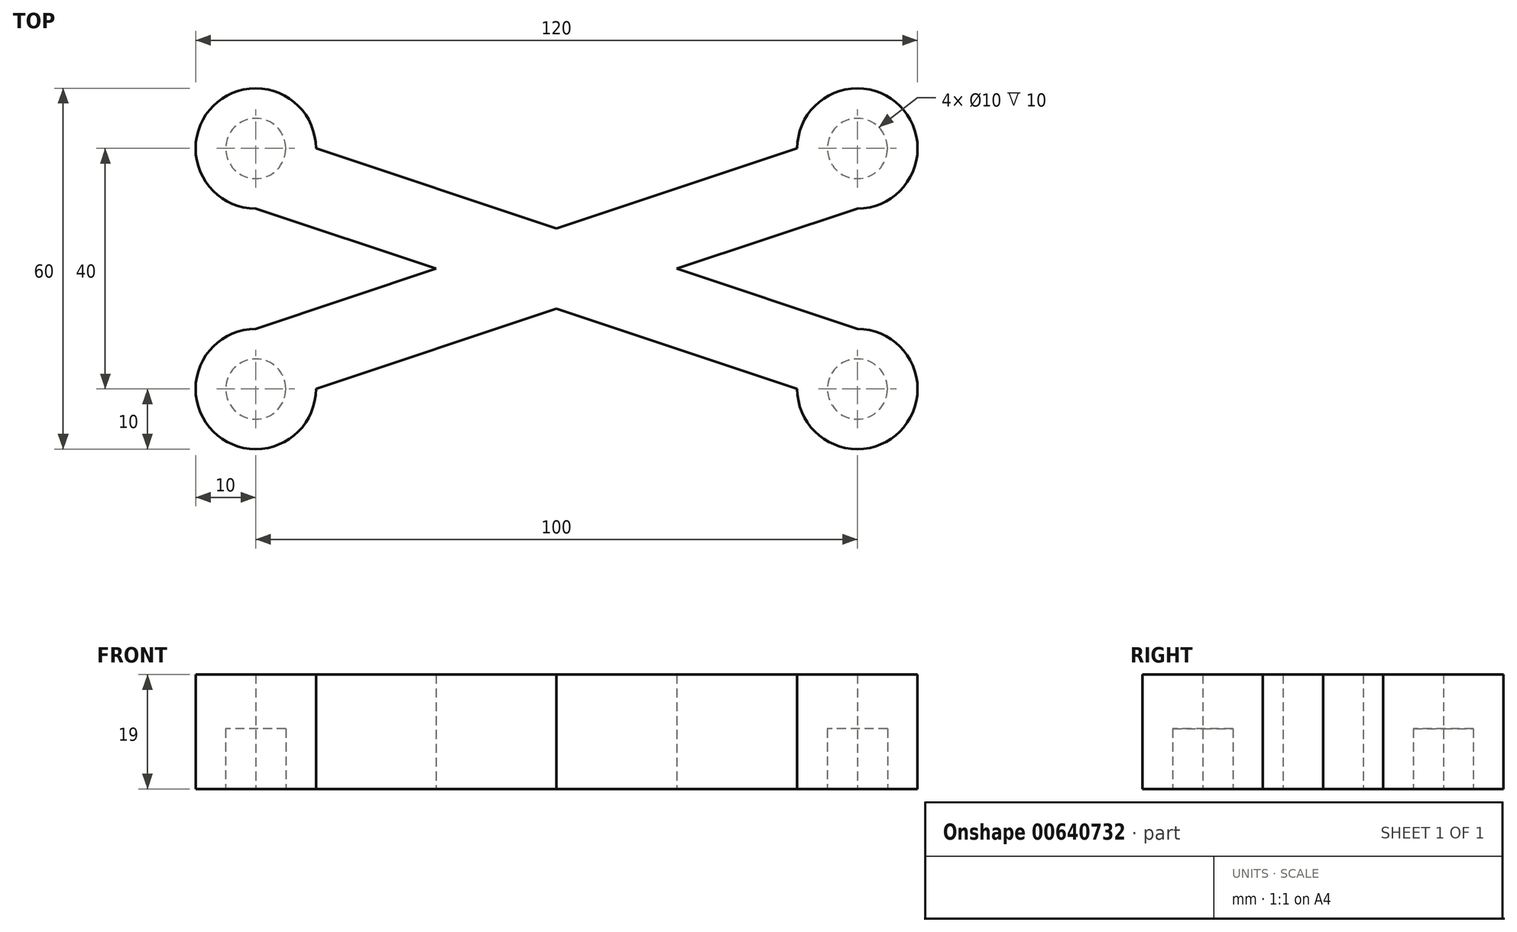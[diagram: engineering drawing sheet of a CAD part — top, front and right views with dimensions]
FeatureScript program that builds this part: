
annotation { "Feature Type Name" : "Feature", "Feature Type Description" : "" }
export const myFeature = defineFeature(function(context is Context, id is Id, definition is map)
    precondition{}
    {
        {
            var Q0;
            Q0=qCreatedBy(makeId("Top.planeOp"),FACE);
            var sketch = newSketch(context, id + "F0", { "sketchPlane" : qUnion([Q0])});
            skLineSegment(sketch, "E0.bottom", {"start": v(-25, 10) * mm, "end": v(25, 10) * mm});
            skLineSegment(sketch, "E0.top", {"start": v(-25, -10) * mm, "end": v(25, -10) * mm});
            skLineSegment(sketch, "E0.left", {"start": v(-25, 10) * mm, "end": v(-25, -10) * mm});
            skLineSegment(sketch, "E0.right", {"start": v(25, 10) * mm, "end": v(25, -10) * mm});
            skPoint(sketch, "E0.middle", {"position": v(0, 0) * mm});
            skLineSegment(sketch, "E1.bottom", {"start": v(0, 0) * mm, "end": v(-50, 0) * mm});
            skLineSegment(sketch, "E1.top", {"start": v(0, 20) * mm, "end": v(-50, 20) * mm});
            skLineSegment(sketch, "E1.left", {"start": v(0, 0) * mm, "end": v(0, 20) * mm});
            skLineSegment(sketch, "E1.right", {"start": v(-50, 0) * mm, "end": v(-50, 20) * mm});
            skPoint(sketch, "E1.middle", {"position": v(-25, 10) * mm});
            skLineSegment(sketch, "E2.bottom", {"start": v(0, 0) * mm, "end": v(50, 0) * mm});
            skLineSegment(sketch, "E2.top", {"start": v(0, 20) * mm, "end": v(50, 20) * mm});
            skLineSegment(sketch, "E2.right", {"start": v(50, 0) * mm, "end": v(50, 20) * mm});
            skPoint(sketch, "E2.middle", {"position": v(25, 10) * mm});
            skLineSegment(sketch, "E3.bottom", {"start": v(-50, 0) * mm, "end": v(0, 0) * mm});
            skLineSegment(sketch, "E3.top", {"start": v(-50, -20) * mm, "end": v(0, -20) * mm});
            skLineSegment(sketch, "E3.left", {"start": v(-50, 0) * mm, "end": v(-50, -20) * mm});
            skLineSegment(sketch, "E3.right", {"start": v(0, 0) * mm, "end": v(0, -20) * mm});
            skPoint(sketch, "E3.middle", {"position": v(-25, -10) * mm});
            skLineSegment(sketch, "E4.bottom", {"start": v(50, 0) * mm, "end": v(0, 0) * mm});
            skLineSegment(sketch, "E4.top", {"start": v(50, -20) * mm, "end": v(0, -20) * mm});
            skLineSegment(sketch, "E4.left", {"start": v(50, 0) * mm, "end": v(50, -20) * mm});
            skPoint(sketch, "E4.middle", {"position": v(25, -10) * mm});
            skCircle(sketch, "E5", {"center": v(-50, 20) * mm, "radius": 10 * mm});
            skCircle(sketch, "E6", {"center": v(-50, -20) * mm, "radius": 10 * mm});
            skCircle(sketch, "E7", {"center": v(50, -20) * mm, "radius": 10 * mm});
            skCircle(sketch, "E8", {"center": v(50, 20) * mm, "radius": 10 * mm});
            skLineSegment(sketch, "E9", {"start": v(-40, 20) * mm, "end": v(50, -10) * mm});
            skLineSegment(sketch, "E10", {"start": v(50, -10) * mm, "end": v(40, -20) * mm});
            skLineSegment(sketch, "E11", {"start": v(-50, 10) * mm, "end": v(40, -20) * mm});
            skLineSegment(sketch, "E12", {"start": v(-50, -10) * mm, "end": v(40, 20) * mm});
            skLineSegment(sketch, "E13", {"start": v(40, 20) * mm, "end": v(50, 10) * mm});
            skLineSegment(sketch, "E14", {"start": v(50, 10) * mm, "end": v(-40, -20) * mm});
            skLineSegment(sketch, "E15", {"start": v(-50, -10) * mm, "end": v(-50, 10) * mm});
            skLineSegment(sketch, "E16", {"start": v(-40, -20) * mm, "end": v(-40, 20) * mm});
            skLineSegment(sketch, "E17", {"start": v(40, -20) * mm, "end": v(40, 20) * mm});
            skSolve(sketch);
        }
        {
            var Q0;
            {var subQ0=sQuery(id+"F0.wireOp",EDGE,"E1.right");Q0=makeQuery(id+"F0.imprint","IMPRINT",FACE,{"disambiguationData":[TD([[makeQuery(id+"F0.imprint","IMPRINT",EDGE,{"derivedFrom":subQ0}),1.0]])]});}
            var Q1;
            {var subQ0=sQuery(id+"F0.wireOp",EDGE,"E2.right");var subQ1=sQuery(id+"F0.wireOp",EDGE,"E2.top");var subQ2=makeQuery(id+"F0.imprint","INTERSECT",VERTEX,{"derivedFrom":[subQ1,subQ0]});Q1=makeQuery(id+"F0.imprint","IMPRINT",FACE,{"disambiguationData":[TD([[makeQuery(id+"F0.imprint","IMPRINT",EDGE,{"disambiguationData":[TD([[subQ2,1.0]])],"derivedFrom":subQ0}),-1.0]])]});}
            var Q2;
            {var subQ0=sQuery(id+"F0.wireOp",EDGE,"E3.left");Q2=makeQuery(id+"F0.imprint","IMPRINT",FACE,{"disambiguationData":[TD([[makeQuery(id+"F0.imprint","IMPRINT",EDGE,{"derivedFrom":subQ0}),-1.0]])]});}
            var Q3;
            {var subQ0=sQuery(id+"F0.wireOp",EDGE,"E4.left");var subQ1=sQuery(id+"F0.wireOp",EDGE,"E4.top");var subQ2=makeQuery(id+"F0.imprint","INTERSECT",VERTEX,{"derivedFrom":[subQ1,subQ0]});Q3=makeQuery(id+"F0.imprint","IMPRINT",FACE,{"disambiguationData":[TD([[makeQuery(id+"F0.imprint","IMPRINT",EDGE,{"disambiguationData":[TD([[subQ2,1.0]])],"derivedFrom":subQ0}),1.0]])]});}
            var Q4;
            {var subQ3=sQuery(id+"F0.wireOp",EDGE,"E10");Q4=makeQuery(id+"F0.imprint","IMPRINT",FACE,{"disambiguationData":[TD([[makeQuery(id+"F0.imprint","IMPRINT",EDGE,{"derivedFrom":subQ3}),1.0]])]});}
            var Q5;
            {var subQ0=sQuery(id+"F0.wireOp",EDGE,"E10");Q5=makeQuery(id+"F0.imprint","IMPRINT",FACE,{"disambiguationData":[TD([[makeQuery(id+"F0.imprint","IMPRINT",EDGE,{"derivedFrom":subQ0}),-1.0]])]});}
            var Q6;
            {var subQ3=sQuery(id+"F0.wireOp",EDGE,"E13");Q6=makeQuery(id+"F0.imprint","IMPRINT",FACE,{"disambiguationData":[TD([[makeQuery(id+"F0.imprint","IMPRINT",EDGE,{"derivedFrom":subQ3}),1.0]])]});}
            var Q7;
            {var subQ0=sQuery(id+"F0.wireOp",EDGE,"E13");Q7=makeQuery(id+"F0.imprint","IMPRINT",FACE,{"disambiguationData":[TD([[makeQuery(id+"F0.imprint","IMPRINT",EDGE,{"derivedFrom":subQ0}),-1.0]])]});}
            var Q8;
            {var subQ0=sQuery(id+"F0.wireOp",EDGE,"E1.right");Q8=makeQuery(id+"F0.imprint","IMPRINT",FACE,{"disambiguationData":[TD([[makeQuery(id+"F0.imprint","IMPRINT",EDGE,{"derivedFrom":subQ0}),-1.0]])]});}
            var Q9;
            {var subQ0=sQuery(id+"F0.wireOp",EDGE,"E3.left");Q9=makeQuery(id+"F0.imprint","IMPRINT",FACE,{"disambiguationData":[TD([[makeQuery(id+"F0.imprint","IMPRINT",EDGE,{"derivedFrom":subQ0}),1.0]])]});}
            var Q10;
            {var subQ0=sQuery(id+"F0.wireOp",EDGE,"E15");var subQ1=sQuery(id+"F0.wireOp",EDGE,"E3.bottom");var subQ2=makeQuery(id+"F0.imprint","INTERSECT",VERTEX,{"derivedFrom":[subQ1,subQ0]});Q10=makeQuery(id+"F0.imprint","IMPRINT",FACE,{"disambiguationData":[TD([[makeQuery(id+"F0.imprint","IMPRINT",EDGE,{"disambiguationData":[TD([[subQ2,-1.0]])],"derivedFrom":subQ1}),-1.0]])]});}
            var Q11;
            {var subQ0=sQuery(id+"F0.wireOp",EDGE,"E15");var subQ1=sQuery(id+"F0.wireOp",EDGE,"E3.bottom");var subQ2=makeQuery(id+"F0.imprint","INTERSECT",VERTEX,{"derivedFrom":[subQ1,subQ0]});Q11=makeQuery(id+"F0.imprint","IMPRINT",FACE,{"disambiguationData":[TD([[makeQuery(id+"F0.imprint","IMPRINT",EDGE,{"disambiguationData":[TD([[subQ2,-1.0]])],"derivedFrom":subQ1}),1.0]])]});}
            var Q12;
            {var subQ0=sQuery(id+"F0.wireOp",EDGE,"E11");var subQ3=sQuery(id+"F0.wireOp",EDGE,"E16");var subQ5=makeQuery(id+"F0.imprint","INTERSECT",VERTEX,{"derivedFrom":[subQ0,subQ3]});Q12=makeQuery(id+"F0.imprint","IMPRINT",FACE,{"disambiguationData":[TD([[makeQuery(id+"F0.imprint","IMPRINT",EDGE,{"disambiguationData":[TD([[subQ5,1.0]])],"derivedFrom":subQ0}),1.0]])]});}
            var Q13;
            {var subQ0=sQuery(id+"F0.wireOp",EDGE,"E12");var subQ3=sQuery(id+"F0.wireOp",EDGE,"E16");var subQ5=makeQuery(id+"F0.imprint","INTERSECT",VERTEX,{"derivedFrom":[subQ0,subQ3]});Q13=makeQuery(id+"F0.imprint","IMPRINT",FACE,{"disambiguationData":[TD([[makeQuery(id+"F0.imprint","IMPRINT",EDGE,{"disambiguationData":[TD([[subQ5,1.0]])],"derivedFrom":subQ0}),-1.0]])]});}
            var Q14;
            {var subQ0=sQuery(id+"F0.wireOp",EDGE,"E17");var subQ4=sQuery(id+"F0.wireOp",EDGE,"E14");var subQ6=makeQuery(id+"F0.imprint","INTERSECT",VERTEX,{"derivedFrom":[subQ4,subQ0]});Q14=makeQuery(id+"F0.imprint","IMPRINT",FACE,{"disambiguationData":[TD([[makeQuery(id+"F0.imprint","IMPRINT",EDGE,{"disambiguationData":[TD([[subQ6,1.0]])],"derivedFrom":subQ4}),-1.0]])]});}
            var Q15;
            {var subQ1=sQuery(id+"F0.wireOp",EDGE,"E9");var subQ4=sQuery(id+"F0.wireOp",EDGE,"E17");var subQ6=makeQuery(id+"F0.imprint","INTERSECT",VERTEX,{"derivedFrom":[subQ1,subQ4]});Q15=makeQuery(id+"F0.imprint","IMPRINT",FACE,{"disambiguationData":[TD([[makeQuery(id+"F0.imprint","IMPRINT",EDGE,{"disambiguationData":[TD([[subQ6,-1.0]])],"derivedFrom":subQ1}),-1.0]])]});}
            var Q16;
            {var subQ1=sQuery(id+"F0.wireOp",EDGE,"E4.bottom");var subQ3=sQuery(id+"F0.wireOp",EDGE,"E17");var subQ4=makeQuery(id+"F0.imprint","INTERSECT",VERTEX,{"derivedFrom":[subQ1,subQ3]});Q16=makeQuery(id+"F0.imprint","IMPRINT",FACE,{"disambiguationData":[TD([[makeQuery(id+"F0.imprint","IMPRINT",EDGE,{"disambiguationData":[TD([[subQ4,1.0]])],"derivedFrom":subQ3}),-1.0]])]});}
            var Q17;
            {var subQ0=sQuery(id+"F0.wireOp",EDGE,"E4.bottom");var subQ5=sQuery(id+"F0.wireOp",EDGE,"E17");var subQ6=makeQuery(id+"F0.imprint","INTERSECT",VERTEX,{"derivedFrom":[subQ0,subQ5]});Q17=makeQuery(id+"F0.imprint","IMPRINT",FACE,{"disambiguationData":[TD([[makeQuery(id+"F0.imprint","IMPRINT",EDGE,{"disambiguationData":[TD([[subQ6,-1.0]])],"derivedFrom":subQ5}),-1.0]])]});}
            var Q18;
            {var subQ3=sQuery(id+"F0.wireOp",EDGE,"E0.bottom");var subQ5=sQuery(id+"F0.wireOp",EDGE,"E0.left");var subQ6=makeQuery(id+"F0.imprint","INTERSECT",VERTEX,{"derivedFrom":[subQ3,subQ5]});Q18=makeQuery(id+"F0.imprint","IMPRINT",FACE,{"disambiguationData":[TD([[makeQuery(id+"F0.imprint","IMPRINT",EDGE,{"disambiguationData":[TD([[subQ6,-1.0]])],"derivedFrom":subQ3}),1.0]])]});}
            var Q19;
            {var subQ3=sQuery(id+"F0.wireOp",EDGE,"E0.bottom");var subQ5=sQuery(id+"F0.wireOp",EDGE,"E0.right");var subQ6=makeQuery(id+"F0.imprint","INTERSECT",VERTEX,{"derivedFrom":[subQ3,subQ5]});Q19=makeQuery(id+"F0.imprint","IMPRINT",FACE,{"disambiguationData":[TD([[makeQuery(id+"F0.imprint","IMPRINT",EDGE,{"disambiguationData":[TD([[subQ6,1.0]])],"derivedFrom":subQ3}),1.0]])]});}
            var Q20;
            {var subQ1=sQuery(id+"F0.wireOp",EDGE,"E1.left");var subQ3=sQuery(id+"F0.wireOp",EDGE,"E9");var subQ4=makeQuery(id+"F0.imprint","INTERSECT",VERTEX,{"derivedFrom":[subQ1,subQ3,sQuery(id+"F0.wireOp",EDGE,"E12")]});Q20=makeQuery(id+"F0.imprint","IMPRINT",FACE,{"disambiguationData":[TD([[makeQuery(id+"F0.imprint","IMPRINT",EDGE,{"disambiguationData":[TD([[subQ4,-1.0]])],"derivedFrom":subQ3}),-1.0]])]});}
            var Q21;
            {var subQ1=sQuery(id+"F0.wireOp",EDGE,"E1.left");var subQ3=sQuery(id+"F0.wireOp",EDGE,"E12");var subQ4=makeQuery(id+"F0.imprint","INTERSECT",VERTEX,{"derivedFrom":[subQ1,sQuery(id+"F0.wireOp",EDGE,"E9"),subQ3]});Q21=makeQuery(id+"F0.imprint","IMPRINT",FACE,{"disambiguationData":[TD([[makeQuery(id+"F0.imprint","IMPRINT",EDGE,{"disambiguationData":[TD([[subQ4,1.0]])],"derivedFrom":subQ3}),-1.0]])]});}
            var Q22;
            {var subQ3=sQuery(id+"F0.wireOp",EDGE,"E0.top");var subQ6=sQuery(id+"F0.wireOp",EDGE,"E0.left");var subQ9=makeQuery(id+"F0.imprint","INTERSECT",VERTEX,{"derivedFrom":[subQ3,subQ6]});Q22=makeQuery(id+"F0.imprint","IMPRINT",FACE,{"disambiguationData":[TD([[makeQuery(id+"F0.imprint","IMPRINT",EDGE,{"disambiguationData":[TD([[subQ9,-1.0]])],"derivedFrom":subQ3}),-1.0]])]});}
            var Q23;
            {var subQ3=sQuery(id+"F0.wireOp",EDGE,"E0.top");var subQ6=sQuery(id+"F0.wireOp",EDGE,"E0.right");var subQ9=makeQuery(id+"F0.imprint","INTERSECT",VERTEX,{"derivedFrom":[subQ3,subQ6]});Q23=makeQuery(id+"F0.imprint","IMPRINT",FACE,{"disambiguationData":[TD([[makeQuery(id+"F0.imprint","IMPRINT",EDGE,{"disambiguationData":[TD([[subQ9,1.0]])],"derivedFrom":subQ3}),-1.0]])]});}
            var Q24;
            {var subQ1=sQuery(id+"F0.wireOp",EDGE,"E4.bottom");var subQ3=sQuery(id+"F0.wireOp",EDGE,"E14");var subQ4=makeQuery(id+"F0.imprint","INTERSECT",VERTEX,{"derivedFrom":[subQ1,sQuery(id+"F0.wireOp",EDGE,"E9"),subQ3]});Q24=makeQuery(id+"F0.imprint","IMPRINT",FACE,{"disambiguationData":[TD([[makeQuery(id+"F0.imprint","IMPRINT",EDGE,{"disambiguationData":[TD([[subQ4,-1.0]])],"derivedFrom":subQ3}),-1.0]])]});}
            var Q25;
            {var subQ1=sQuery(id+"F0.wireOp",EDGE,"E3.bottom");var subQ3=sQuery(id+"F0.wireOp",EDGE,"E11");var subQ4=makeQuery(id+"F0.imprint","INTERSECT",VERTEX,{"derivedFrom":[subQ1,subQ3,sQuery(id+"F0.wireOp",EDGE,"E12")]});Q25=makeQuery(id+"F0.imprint","IMPRINT",FACE,{"disambiguationData":[TD([[makeQuery(id+"F0.imprint","IMPRINT",EDGE,{"disambiguationData":[TD([[subQ4,-1.0]])],"derivedFrom":subQ3}),1.0]])]});}
            var Q26;
            {var subQ1=sQuery(id+"F0.wireOp",EDGE,"E0.top");var subQ6=sQuery(id+"F0.wireOp",EDGE,"E0.right");var subQ9=makeQuery(id+"F0.imprint","INTERSECT",VERTEX,{"derivedFrom":[subQ1,subQ6]});Q26=makeQuery(id+"F0.imprint","IMPRINT",FACE,{"disambiguationData":[TD([[makeQuery(id+"F0.imprint","IMPRINT",EDGE,{"disambiguationData":[TD([[subQ9,1.0]])],"derivedFrom":subQ1}),1.0]])]});}
            var Q27;
            {var subQ1=sQuery(id+"F0.wireOp",EDGE,"E0.bottom");var subQ5=sQuery(id+"F0.wireOp",EDGE,"E0.right");var subQ6=makeQuery(id+"F0.imprint","INTERSECT",VERTEX,{"derivedFrom":[subQ1,subQ5]});Q27=makeQuery(id+"F0.imprint","IMPRINT",FACE,{"disambiguationData":[TD([[makeQuery(id+"F0.imprint","IMPRINT",EDGE,{"disambiguationData":[TD([[subQ6,1.0]])],"derivedFrom":subQ1}),-1.0]])]});}
            var Q28;
            {var subQ1=sQuery(id+"F0.wireOp",EDGE,"E0.left");var subQ6=sQuery(id+"F0.wireOp",EDGE,"E0.bottom");var subQ9=makeQuery(id+"F0.imprint","INTERSECT",VERTEX,{"derivedFrom":[subQ6,subQ1]});Q28=makeQuery(id+"F0.imprint","IMPRINT",FACE,{"disambiguationData":[TD([[makeQuery(id+"F0.imprint","IMPRINT",EDGE,{"disambiguationData":[TD([[subQ9,-1.0]])],"derivedFrom":subQ6}),-1.0]])]});}
            var Q29;
            {var subQ1=sQuery(id+"F0.wireOp",EDGE,"E0.left");var subQ7=sQuery(id+"F0.wireOp",EDGE,"E0.top");var subQ8=makeQuery(id+"F0.imprint","INTERSECT",VERTEX,{"derivedFrom":[subQ7,subQ1]});Q29=makeQuery(id+"F0.imprint","IMPRINT",FACE,{"disambiguationData":[TD([[makeQuery(id+"F0.imprint","IMPRINT",EDGE,{"disambiguationData":[TD([[subQ8,-1.0]])],"derivedFrom":subQ7}),1.0]])]});}
            extrude(context, id + "F1", {"entities" : qUnion([Q0, Q1, Q2, Q3, Q4, Q5, Q6, Q7, Q8, Q9, Q10, Q11, Q12, Q13, Q14, Q15, Q16, Q17, Q18, Q19, Q20, Q21, Q22, Q23, Q24, Q25, Q26, Q27, Q28, Q29]), "depth" : 19 * mm, "offsetDistance" : 25 * mm});
        }
        {
            var Q0;
            Q0=qCreatedBy(makeId("Top.planeOp"),FACE);
            var sketch = newSketch(context, id + "F2", { "sketchPlane" : qUnion([Q0])});
            skLineSegment(sketch, "E18.bottom", {"start": v(-50, -20) * mm, "end": v(50, -20) * mm});
            skLineSegment(sketch, "E18.top", {"start": v(-50, 20) * mm, "end": v(50, 20) * mm});
            skLineSegment(sketch, "E18.left", {"start": v(-50, -20) * mm, "end": v(-50, 20) * mm});
            skLineSegment(sketch, "E18.right", {"start": v(50, -20) * mm, "end": v(50, 20) * mm});
            skPoint(sketch, "E18.middle", {"position": v(0, 0) * mm});
            skCircle(sketch, "E19", {"center": v(-50, -20) * mm, "radius": 5 * mm});
            skCircle(sketch, "E20", {"center": v(50, -20) * mm, "radius": 5 * mm});
            skCircle(sketch, "E21", {"center": v(50, 20) * mm, "radius": 5 * mm});
            skCircle(sketch, "E22", {"center": v(-50, 20) * mm, "radius": 5 * mm});
            skSolve(sketch);
        }
        {
            var Q0;
            {var subQ0=sQuery(id+"F2.wireOp",EDGE,"E18.left");var subQ1=sQuery(id+"F2.wireOp",EDGE,"E18.bottom");var subQ2=makeQuery(id+"F2.imprint","INTERSECT",VERTEX,{"derivedFrom":[subQ1,subQ0]});Q0=makeQuery(id+"F2.imprint","IMPRINT",FACE,{"disambiguationData":[TD([[makeQuery(id+"F2.imprint","IMPRINT",EDGE,{"disambiguationData":[TD([[subQ2,-1.0]])],"derivedFrom":subQ1}),-1.0]])]});}
            var Q1;
            {var subQ0=sQuery(id+"F2.wireOp",EDGE,"E18.left");var subQ1=sQuery(id+"F2.wireOp",EDGE,"E18.bottom");var subQ2=makeQuery(id+"F2.imprint","INTERSECT",VERTEX,{"derivedFrom":[subQ1,subQ0]});Q1=makeQuery(id+"F2.imprint","IMPRINT",FACE,{"disambiguationData":[TD([[makeQuery(id+"F2.imprint","IMPRINT",EDGE,{"disambiguationData":[TD([[subQ2,-1.0]])],"derivedFrom":subQ1}),1.0]])]});}
            var Q2;
            {var subQ0=sQuery(id+"F2.wireOp",EDGE,"E18.left");var subQ1=sQuery(id+"F2.wireOp",EDGE,"E18.top");var subQ2=makeQuery(id+"F2.imprint","INTERSECT",VERTEX,{"derivedFrom":[subQ1,subQ0]});Q2=makeQuery(id+"F2.imprint","IMPRINT",FACE,{"disambiguationData":[TD([[makeQuery(id+"F2.imprint","IMPRINT",EDGE,{"disambiguationData":[TD([[subQ2,-1.0]])],"derivedFrom":subQ1}),-1.0]])]});}
            var Q3;
            {var subQ0=sQuery(id+"F2.wireOp",EDGE,"E18.left");var subQ1=sQuery(id+"F2.wireOp",EDGE,"E18.top");var subQ2=makeQuery(id+"F2.imprint","INTERSECT",VERTEX,{"derivedFrom":[subQ1,subQ0]});Q3=makeQuery(id+"F2.imprint","IMPRINT",FACE,{"disambiguationData":[TD([[makeQuery(id+"F2.imprint","IMPRINT",EDGE,{"disambiguationData":[TD([[subQ2,-1.0]])],"derivedFrom":subQ1}),1.0]])]});}
            var Q4;
            {var subQ0=sQuery(id+"F2.wireOp",EDGE,"E18.right");var subQ1=sQuery(id+"F2.wireOp",EDGE,"E18.bottom");var subQ2=makeQuery(id+"F2.imprint","INTERSECT",VERTEX,{"derivedFrom":[subQ1,subQ0]});Q4=makeQuery(id+"F2.imprint","IMPRINT",FACE,{"disambiguationData":[TD([[makeQuery(id+"F2.imprint","IMPRINT",EDGE,{"disambiguationData":[TD([[subQ2,1.0]])],"derivedFrom":subQ1}),1.0]])]});}
            var Q5;
            {var subQ0=sQuery(id+"F2.wireOp",EDGE,"E18.right");var subQ1=sQuery(id+"F2.wireOp",EDGE,"E18.bottom");var subQ2=makeQuery(id+"F2.imprint","INTERSECT",VERTEX,{"derivedFrom":[subQ1,subQ0]});Q5=makeQuery(id+"F2.imprint","IMPRINT",FACE,{"disambiguationData":[TD([[makeQuery(id+"F2.imprint","IMPRINT",EDGE,{"disambiguationData":[TD([[subQ2,1.0]])],"derivedFrom":subQ1}),-1.0]])]});}
            var Q6;
            {var subQ0=sQuery(id+"F2.wireOp",EDGE,"E18.right");var subQ1=sQuery(id+"F2.wireOp",EDGE,"E18.top");var subQ2=makeQuery(id+"F2.imprint","INTERSECT",VERTEX,{"derivedFrom":[subQ1,subQ0]});Q6=makeQuery(id+"F2.imprint","IMPRINT",FACE,{"disambiguationData":[TD([[makeQuery(id+"F2.imprint","IMPRINT",EDGE,{"disambiguationData":[TD([[subQ2,1.0]])],"derivedFrom":subQ1}),1.0]])]});}
            var Q7;
            {var subQ0=sQuery(id+"F2.wireOp",EDGE,"E18.right");var subQ1=sQuery(id+"F2.wireOp",EDGE,"E18.top");var subQ2=makeQuery(id+"F2.imprint","INTERSECT",VERTEX,{"derivedFrom":[subQ1,subQ0]});Q7=makeQuery(id+"F2.imprint","IMPRINT",FACE,{"disambiguationData":[TD([[makeQuery(id+"F2.imprint","IMPRINT",EDGE,{"disambiguationData":[TD([[subQ2,1.0]])],"derivedFrom":subQ1}),-1.0]])]});}
            extrude(context, id + "F3", {"entities" : qUnion([Q0, Q1, Q2, Q3, Q4, Q5, Q6, Q7]), "operationType" : NewBodyOperationType.REMOVE, "depth" : 10 * mm, "offsetDistance" : 25 * mm});
        }
    });
